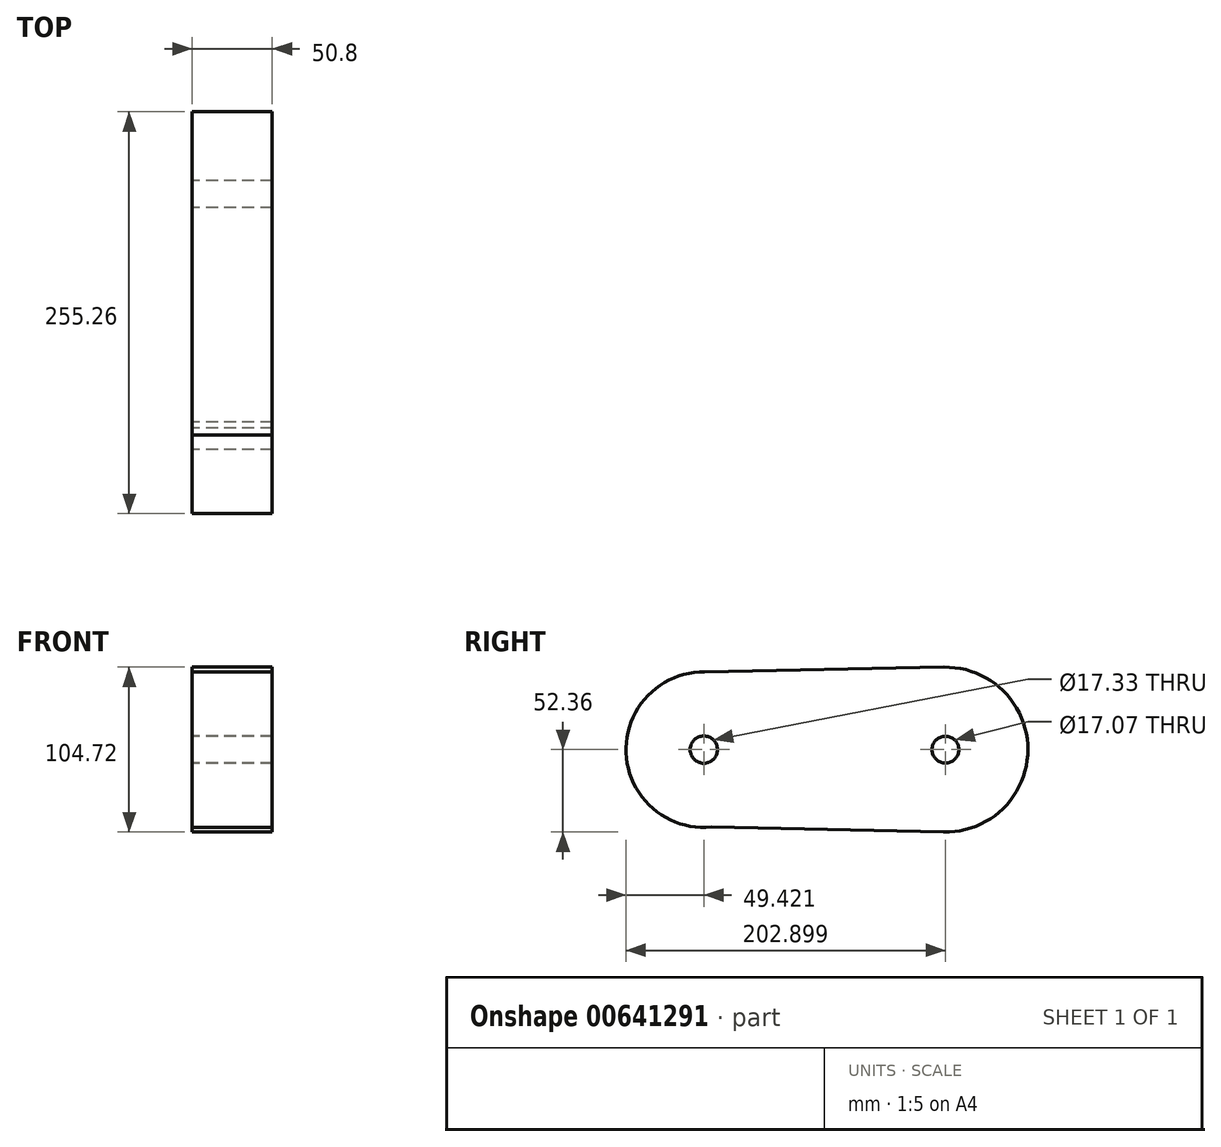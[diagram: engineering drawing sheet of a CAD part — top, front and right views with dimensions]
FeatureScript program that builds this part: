
annotation { "Feature Type Name" : "Feature", "Feature Type Description" : "" }
export const myFeature = defineFeature(function(context is Context, id is Id, definition is map)
    precondition{}
    {
        {
            var Q0;
            Q0=qCreatedBy(makeId("Right.planeOp"),FACE);
            var sketch = newSketch(context, id + "F0", { "sketchPlane" : qUnion([Q0])});
            skCircle(sketch, "E0", {"center": v(-81.5, 0) * mm, "radius": 49.42 * mm});
            skCircle(sketch, "E1", {"center": v(71.97, 0) * mm, "radius": 52.36 * mm});
            skLineSegment(sketch, "E2", {"start": v(-80.94, 49.42) * mm, "end": v(70.96, 52.35) * mm});
            skLineSegment(sketch, "E3", {"start": v(70.96, 52.35) * mm, "end": v(70.96, 52.35) * mm});
            skLineSegment(sketch, "E4", {"start": v(-76.66, -49.19) * mm, "end": v(70.85, -52.35) * mm});
            skCircle(sketch, "E5", {"center": v(-81.5, 0) * mm, "radius": 8.67 * mm});
            skCircle(sketch, "E6", {"center": v(71.97, 0) * mm, "radius": 8.53 * mm});
            skSolve(sketch);
        }
        {
            var Q0;
            Q0 = qSketchRegion(id + "F0", true);
            extrude(context, id + "F1", {"entities" : qUnion([Q0]), "depth" : 50.8 * mm, "offsetDistance" : 25.4 * mm});
        }
    });
